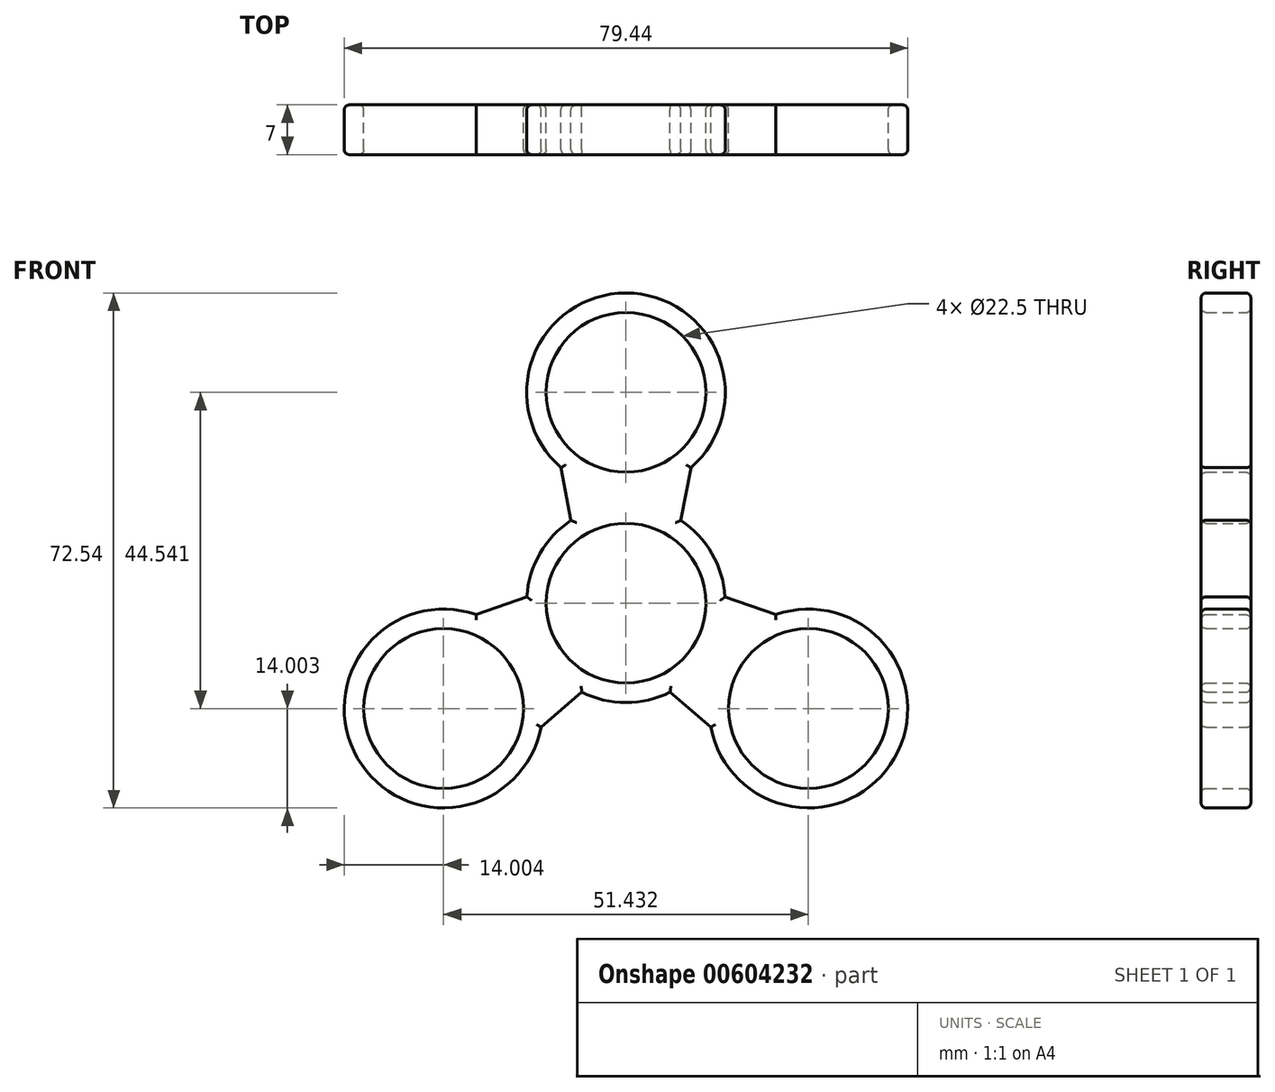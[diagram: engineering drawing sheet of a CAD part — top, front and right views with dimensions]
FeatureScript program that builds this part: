
annotation { "Feature Type Name" : "Feature", "Feature Type Description" : "" }
export const myFeature = defineFeature(function(context is Context, id is Id, definition is map)
    precondition{}
    {
        {
            var Q0;
            Q0=qCreatedBy(makeId("Front.planeOp"),FACE);
            var sketch = newSketch(context, id + "F0", { "sketchPlane" : qUnion([Q0])});
            skCircle(sketch, "E0", {"center": v(0, 0) * mm, "radius": 11.25 * mm});
            skCircle(sketch, "E1", {"center": v(0, 0) * mm, "radius": 14 * mm});
            skCircle(sketch, "E2", {"center": v(0, 29.7) * mm, "radius": 11.25 * mm});
            skCircle(sketch, "E3", {"center": v(0, 29.7) * mm, "radius": 14 * mm});
            skPoint(sketch, "E4", {"position": v(0, 15.7) * mm});
            skPoint(sketch, "E5", {"position": v(9.15, 19.1) * mm});
            skPoint(sketch, "E6", {"position": v(-9.15, 19.1) * mm});
            skPoint(sketch, "E7", {"position": v(-7.75, 11.66) * mm});
            skPoint(sketch, "E8", {"position": v(7.75, 11.66) * mm});
            skLineSegment(sketch, "E9", {"start": v(-9.15, 19.1) * mm, "end": v(-7.75, 11.66) * mm});
            skLineSegment(sketch, "E10", {"start": v(9.15, 19.1) * mm, "end": v(7.75, 11.66) * mm});
            skCircle(sketch, "E11.1.0", {"center": v(25.72, -14.85) * mm, "radius": 11.25 * mm});
            skCircle(sketch, "E11.1.1", {"center": v(25.72, -14.85) * mm, "radius": 14 * mm});
            skLineSegment(sketch, "E11.1.2", {"start": v(11.96, -17.48) * mm, "end": v(6.22, -12.54) * mm});
            skLineSegment(sketch, "E11.1.3", {"start": v(21.12, -1.62) * mm, "end": v(13.97, 0.88) * mm});
            skCircle(sketch, "E11.2.0", {"center": v(-25.72, -14.85) * mm, "radius": 11.25 * mm});
            skCircle(sketch, "E11.2.1", {"center": v(-25.72, -14.85) * mm, "radius": 14 * mm});
            skLineSegment(sketch, "E11.2.2", {"start": v(-21.12, -1.62) * mm, "end": v(-13.97, 0.88) * mm});
            skLineSegment(sketch, "E11.2.3", {"start": v(-11.96, -17.48) * mm, "end": v(-6.22, -12.54) * mm});
            skLineSegment(sketch, "E11.anchor1", {"start": v(0, 0) * mm, "end": v(-7.75, 11.66) * mm, "construction": true});
            skLineSegment(sketch, "E11.anchor2", {"start": v(0, 0) * mm, "end": v(-6.22, -12.54) * mm, "construction": true});
            skSolve(sketch);
        }
        {
            var Q0;
            Q0 = qSketchRegion(id + "F0", true);
            extrude(context, id + "F1", {"entities" : qUnion([Q0]), "depth" : 7 * mm, "offsetDistance" : 25 * mm});
        }
        {
            var Q0;
            Q0=makeQuery(id+"F1.opExtrude","CAP_FACE",FACE,{"disambiguationData":[OSD([sQuery(id+"F0.wireOp",EDGE,"E0"),sQuery(id+"F0.wireOp",EDGE,"E2"),sQuery(id+"F0.wireOp",EDGE,"E3"),sQuery(id+"F0.wireOp",EDGE,"E9"),sQuery(id+"F0.wireOp",EDGE,"E10"),sQuery(id+"F0.wireOp",EDGE,"E11.1.0"),sQuery(id+"F0.wireOp",EDGE,"E11.1.1"),sQuery(id+"F0.wireOp",EDGE,"E11.1.2"),sQuery(id+"F0.wireOp",EDGE,"E11.1.3"),sQuery(id+"F0.wireOp",EDGE,"E11.2.0"),sQuery(id+"F0.wireOp",EDGE,"E11.2.1"),sQuery(id+"F0.wireOp",EDGE,"E11.2.2"),sQuery(id+"F0.wireOp",EDGE,"E11.2.3"),sQuery(id+"F0.wireOp",EDGE,"E1")])],"isStart":true});
            fillet(context, id + "F2", {"entities" : qUnion([Q0]), "radius" : .7 * mm, "tangentPropagation" : true, "allowEdgeOverflow" : false});
        }
        {
            var Q0;
            Q0=makeQuery(id+"F1.opExtrude","CAP_FACE",FACE,{"disambiguationData":[OSD([sQuery(id+"F0.wireOp",EDGE,"E0"),sQuery(id+"F0.wireOp",EDGE,"E2"),sQuery(id+"F0.wireOp",EDGE,"E3"),sQuery(id+"F0.wireOp",EDGE,"E9"),sQuery(id+"F0.wireOp",EDGE,"E10"),sQuery(id+"F0.wireOp",EDGE,"E11.1.0"),sQuery(id+"F0.wireOp",EDGE,"E11.1.1"),sQuery(id+"F0.wireOp",EDGE,"E11.1.2"),sQuery(id+"F0.wireOp",EDGE,"E11.1.3"),sQuery(id+"F0.wireOp",EDGE,"E11.2.0"),sQuery(id+"F0.wireOp",EDGE,"E11.2.1"),sQuery(id+"F0.wireOp",EDGE,"E11.2.2"),sQuery(id+"F0.wireOp",EDGE,"E11.2.3"),sQuery(id+"F0.wireOp",EDGE,"E1")])],"isStart":false});
            fillet(context, id + "F3", {"entities" : qUnion([Q0]), "radius" : .7 * mm, "tangentPropagation" : true, "allowEdgeOverflow" : false});
        }
    });
